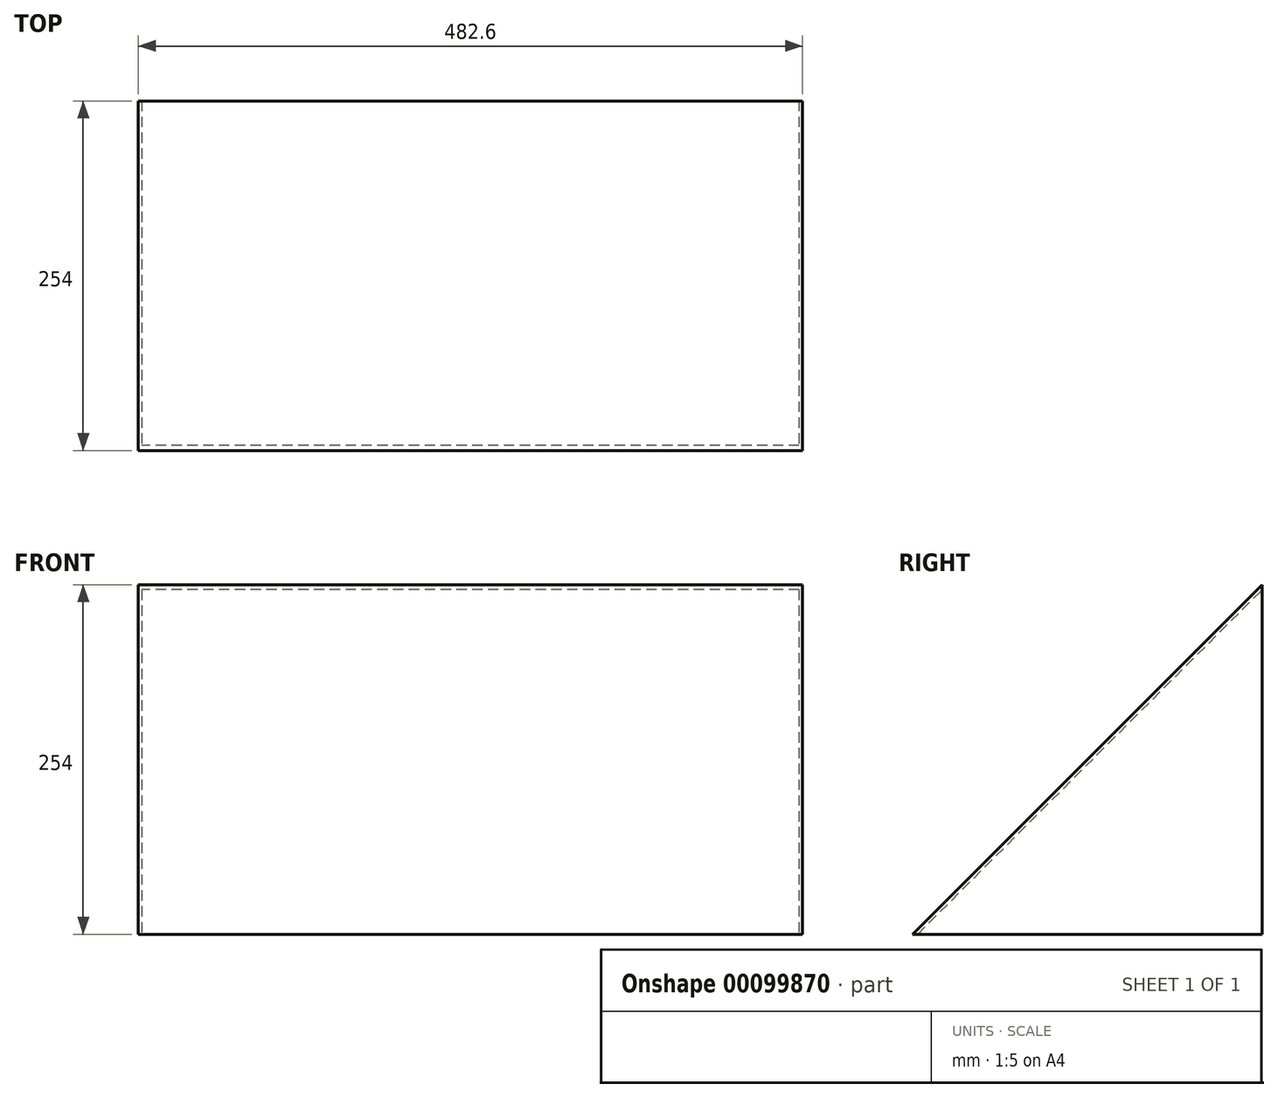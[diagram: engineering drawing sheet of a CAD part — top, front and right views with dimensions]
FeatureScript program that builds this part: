
annotation { "Feature Type Name" : "Feature", "Feature Type Description" : "" }
export const myFeature = defineFeature(function(context is Context, id is Id, definition is map)
    precondition{}
    {
        {
            var Q0;
            Q0=qCreatedBy(makeId("Right.planeOp"),FACE);
            var sketch = newSketch(context, id + "F0", { "sketchPlane" : qUnion([Q0])});
            skLineSegment(sketch, "E0", {"start": v(0, 0) * mm, "end": v(-254, 0) * mm});
            skLineSegment(sketch, "E1", {"start": v(-254, 0) * mm, "end": v(0, 254) * mm});
            skLineSegment(sketch, "E2", {"start": v(0, 254) * mm, "end": v(0, 0) * mm});
            skSolve(sketch);
        }
        {
            var Q0;
            Q0 = qSketchRegion(id + "F0", true);
            extrude(context, id + "F1", {"entities" : qUnion([Q0]), "endBound" : BoundingType.SYMMETRIC, "depth" : 482.6 * mm});
        }
        {
            var Q0;
            Q0=makeQuery(id+"F1.opExtrude","SWEPT_FACE",FACE,{"disambiguationData":[OSD([sQuery(id+"F0.wireOp",EDGE,"E2")])]});
            var Q1;
            Q1=makeQuery(id+"F1.opExtrude","SWEPT_FACE",FACE,{"disambiguationData":[OSD([sQuery(id+"F0.wireOp",EDGE,"E0")])]});
            shell(context, id + "F2", {"entities" : qUnion([Q0, Q1]), "thickness" : 2.54 * mm});
        }
    });
